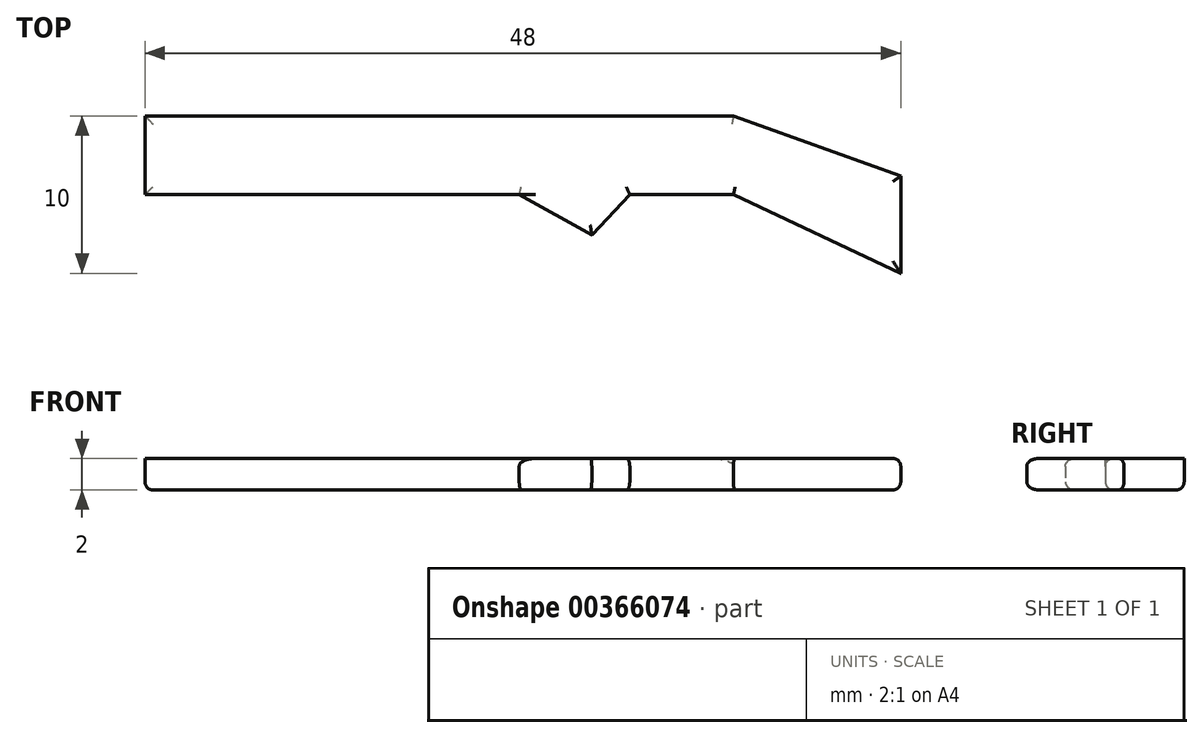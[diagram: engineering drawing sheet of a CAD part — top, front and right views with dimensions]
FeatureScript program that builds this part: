
annotation { "Feature Type Name" : "Feature", "Feature Type Description" : "" }
export const myFeature = defineFeature(function(context is Context, id is Id, definition is map)
    precondition{}
    {
        {
            var Q0;
            Q0=qCreatedBy(makeId("Top.planeOp"),FACE);
            var sketch = newSketch(context, id + "F0", { "sketchPlane" : qUnion([Q0])});
            skLineSegment(sketch, "E0.bottom", {"start": v(0, 0) * mm, "end": v(37.37, 0) * mm});
            skLineSegment(sketch, "E0.left", {"start": v(0, 0) * mm, "end": v(0, -5) * mm});
            skLineSegment(sketch, "E0.right", {"start": v(48, -3.82) * mm, "end": v(48, -10) * mm});
            skLineSegment(sketch, "E1", {"start": v(0, -5) * mm, "end": v(23.77, -5) * mm});
            skPoint(sketch, "E1.endSnap0", {"position": v(0, -5) * mm});
            skLineSegment(sketch, "E2", {"start": v(23.77, -5) * mm, "end": v(28.38, -7.55) * mm});
            skLineSegment(sketch, "E3", {"start": v(28.38, -7.55) * mm, "end": v(30.79, -5) * mm});
            skLineSegment(sketch, "E4", {"start": v(30.79, -5) * mm, "end": v(37.37, -5) * mm});
            skLineSegment(sketch, "E5", {"start": v(37.37, -5) * mm, "end": v(48, -10) * mm});
            skLineSegment(sketch, "E6", {"start": v(37.37, 0) * mm, "end": v(48, -3.82) * mm});
            skPoint(sketch, "E7.orphan", {"position": v(0, -10) * mm});
            skSolve(sketch);
        }
        {
            var Q0;
            Q0=makeQuery(id+"F0.imprint","IMPRINT",FACE,{"disambiguationData":[TD([[makeQuery(id+"F0.imprint","IMPRINT",EDGE,{"derivedFrom":sQuery(id+"F0.wireOp",EDGE,"E0.bottom")}),-1.0]])]});
            extrude(context, id + "F1", {"entities" : qUnion([Q0]), "depth" : 2 * mm});
        }
        {
            var Q0;
            Q0=makeQuery(id+"F1.opExtrude","CAP_EDGE",EDGE,{"disambiguationData":[OSD([sQuery(id+"F0.wireOp",EDGE,"E0.right")])],"isStart":false});
            var Q1;
            Q1=makeQuery(id+"F1.opExtrude","CAP_EDGE",EDGE,{"disambiguationData":[OSD([sQuery(id+"F0.wireOp",EDGE,"E5")])],"isStart":false});
            var Q2;
            Q2=makeQuery(id+"F1.opExtrude","CAP_EDGE",EDGE,{"disambiguationData":[OSD([sQuery(id+"F0.wireOp",EDGE,"E4")])],"isStart":false});
            var Q3;
            Q3=makeQuery(id+"F1.opExtrude","CAP_EDGE",EDGE,{"disambiguationData":[OSD([sQuery(id+"F0.wireOp",EDGE,"E3")])],"isStart":false});
            var Q4;
            Q4=makeQuery(id+"F1.opExtrude","CAP_EDGE",EDGE,{"disambiguationData":[OSD([sQuery(id+"F0.wireOp",EDGE,"E2")])],"isStart":false});
            var Q5;
            Q5=makeQuery(id+"F1.opExtrude","CAP_EDGE",EDGE,{"disambiguationData":[OSD([sQuery(id+"F0.wireOp",EDGE,"E6")])],"isStart":false});
            fillet(context, id + "F2", {"entities" : qUnion([Q0, Q1, Q2, Q3, Q4, Q5]), "radius" : .5 * mm, "tangentPropagation" : true, "allowEdgeOverflow" : false});
        }
        {
            var Q0;
            Q0=makeQuery(id+"F1.opExtrude","CAP_EDGE",EDGE,{"disambiguationData":[OSD([sQuery(id+"F0.wireOp",EDGE,"E1")])],"isStart":true});
            var Q1;
            Q1=makeQuery(id+"F1.opExtrude","CAP_EDGE",EDGE,{"disambiguationData":[OSD([sQuery(id+"F0.wireOp",EDGE,"E2")])],"isStart":true});
            var Q2;
            Q2=makeQuery(id+"F1.opExtrude","CAP_EDGE",EDGE,{"disambiguationData":[OSD([sQuery(id+"F0.wireOp",EDGE,"E3")])],"isStart":true});
            var Q3;
            Q3=makeQuery(id+"F1.opExtrude","CAP_EDGE",EDGE,{"disambiguationData":[OSD([sQuery(id+"F0.wireOp",EDGE,"E4")])],"isStart":true});
            var Q4;
            Q4=makeQuery(id+"F1.opExtrude","CAP_EDGE",EDGE,{"disambiguationData":[OSD([sQuery(id+"F0.wireOp",EDGE,"E5")])],"isStart":true});
            var Q5;
            Q5=makeQuery(id+"F1.opExtrude","CAP_EDGE",EDGE,{"disambiguationData":[OSD([sQuery(id+"F0.wireOp",EDGE,"E0.bottom")])],"isStart":true});
            var Q6;
            Q6=makeQuery(id+"F1.opExtrude","CAP_EDGE",EDGE,{"disambiguationData":[OSD([sQuery(id+"F0.wireOp",EDGE,"E6")])],"isStart":true});
            var Q7;
            Q7=makeQuery(id+"F1.opExtrude","CAP_FACE",FACE,{"disambiguationData":[OSD([sQuery(id+"F0.wireOp",EDGE,"E0.bottom"),sQuery(id+"F0.wireOp",EDGE,"E0.left"),sQuery(id+"F0.wireOp",EDGE,"E0.right"),sQuery(id+"F0.wireOp",EDGE,"E1"),sQuery(id+"F0.wireOp",EDGE,"E2"),sQuery(id+"F0.wireOp",EDGE,"E3"),sQuery(id+"F0.wireOp",EDGE,"E4"),sQuery(id+"F0.wireOp",EDGE,"E5"),sQuery(id+"F0.wireOp",EDGE,"E6")])],"isStart":true});
            fillet(context, id + "F3", {"entities" : qUnion([Q0, Q1, Q2, Q3, Q4, Q5, Q6, Q7]), "radius" : .5 * mm, "tangentPropagation" : true, "allowEdgeOverflow" : false});
        }
    });
